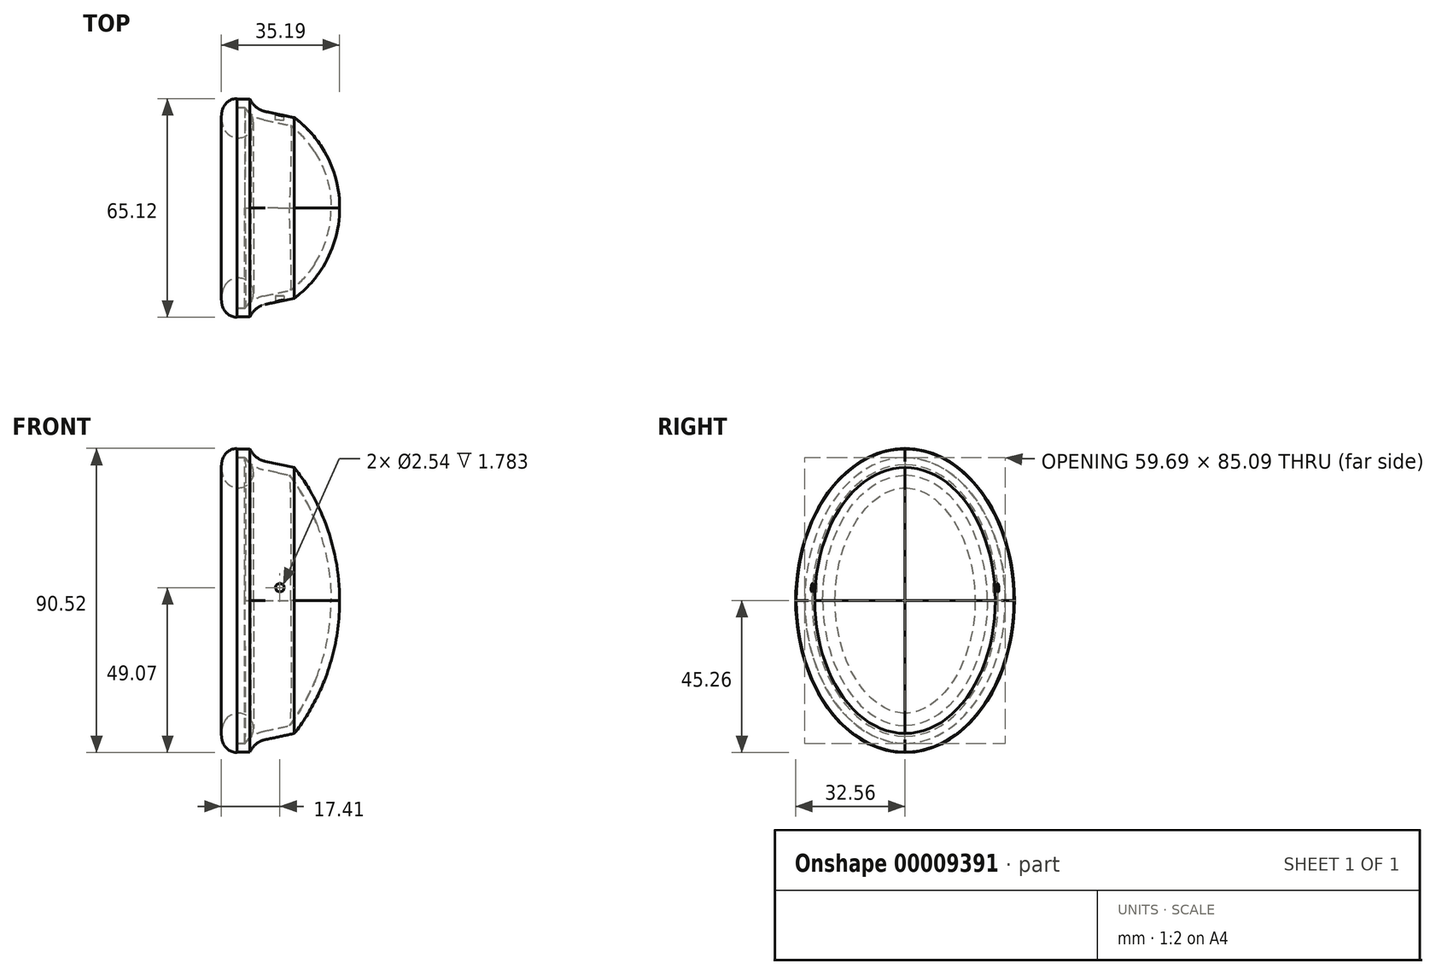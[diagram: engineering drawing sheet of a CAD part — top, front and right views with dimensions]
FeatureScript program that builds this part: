
annotation { "Feature Type Name" : "Feature", "Feature Type Description" : "" }
export const myFeature = defineFeature(function(context is Context, id is Id, definition is map)
    precondition{}
    {
        {
            var Q0;
            Q0=qCreatedBy(makeId("Front.planeOp"),FACE);
            var sketch = newSketch(context, id + "F0", { "sketchPlane" : qUnion([Q0])});
            skLineSegment(sketch, "E0", {"start": v(0, 45.09) * mm, "end": v(3.81, 45.09) * mm});
            skArc(sketch, "E1", {"start": v(3.81, 45.09) * mm, "mid": v(5.62, 42.7) * mm, "end": v(8.3, 41.41) * mm});
            skLineSegment(sketch, "E2", {"start": v(8.3, 41.41) * mm, "end": v(17, 39.57) * mm});
            skArc(sketch, "E3", {"start": v(30.48, 0) * mm, "mid": v(27.02, 20.9) * mm, "end": v(17, 39.57) * mm});
            skLineSegment(sketch, "E4", {"start": v(-135.5, 0) * mm, "end": v(142.56, 0) * mm, "construction": true});
            skLineSegment(sketch, "E5", {"start": v(0, 45.09) * mm, "end": v(0, 0) * mm});
            skLineSegment(sketch, "E6", {"start": v(30.48, 0) * mm, "end": v(0, 0) * mm});
            skSolve(sketch);
        }
        {
            var Q0;
            Q0=qCreatedBy(makeId("Right.planeOp"),FACE);
            var sketch = newSketch(context, id + "F1", { "sketchPlane" : qUnion([Q0])});
            skEllipticalArc(sketch, "E7", {});
            skLineSegment(sketch, "E8", {"start": v(-44.2, 0) * mm, "end": v(67.96, 0) * mm, "construction": true});
            skLineSegment(sketch, "E9", {"start": v(0, 0) * mm, "end": v(0, 53.19) * mm, "construction": true});
            const initialGuessF1  = {"E7": [0, 0, 0, 1, 0.045085, 0.032385, 0, 1.5707963267948966]};
            skSetInitialGuess(sketch, initialGuessF1);
            skSolve(sketch);
        }
        {
            var Q0;
            Q0=qCreatedBy(makeId("Top.planeOp"),FACE);
            var sketch = newSketch(context, id + "F2", { "sketchPlane" : qUnion([Q0])});
            skLineSegment(sketch, "E10", {"start": v(0, 0) * mm, "end": v(0, -32.39) * mm});
            skLineSegment(sketch, "E11", {"start": v(0, -32.39) * mm, "end": v(3.81, -32.39) * mm});
            skArc(sketch, "E12", {"start": v(8.3, -28.71) * mm, "mid": v(5.62, -30) * mm, "end": v(3.81, -32.39) * mm});
            skLineSegment(sketch, "E13", {"start": v(8.3, -28.71) * mm, "end": v(17, -26.87) * mm});
            skArc(sketch, "E14", {"start": v(17, -26.87) * mm, "mid": v(26.92, -15.03) * mm, "end": v(30.48, 0) * mm});
            skLineSegment(sketch, "E15", {"start": v(30.48, 0) * mm, "end": v(0, 0) * mm});
            skSolve(sketch);
        }
        {
            var Q0;
            Q0=qCreatedBy(makeId("Right.planeOp"),FACE);
            var Q1;
            Q1=sQuery(id+"F0.wireOp",VERTEX,"E1.start");
            cPlane(context, id + "F3", {"entities" : qUnion([Q0, Q1]), "cplaneType" : CPlaneType.PLANE_POINT, "offset" : 152.4 * mm, "width" : 152.4 * mm, "height" : 152.4 * mm});
        }
        {
            var Q0;
            Q0=qCreatedBy(id+"F3.planeOp",FACE);
            var sketch = newSketch(context, id + "F4", { "sketchPlane" : qUnion([Q0])});
            skEllipticalArc(sketch, "E16", {});
            skLineSegment(sketch, "E17", {"start": v(0, 0) * mm, "end": v(-53.23, 0) * mm, "construction": true});
            skLineSegment(sketch, "E18", {"start": v(0, 0) * mm, "end": v(0, 51.02) * mm, "construction": true});
            const initialGuessF4  = {"E16": [0, 0, 0, 1, 0.045085, 0.032385, 0, 1.5707963267948966]};
            skSetInitialGuess(sketch, initialGuessF4);
            skSolve(sketch);
        }
        {
            var Q0;
            Q0=qCreatedBy(id+"F3.planeOp",FACE);
            var Q1;
            Q1=sQuery(id+"F0.wireOp",VERTEX,"E2.start");
            cPlane(context, id + "F5", {"entities" : qUnion([Q0, Q1]), "cplaneType" : CPlaneType.PLANE_POINT, "offset" : 152.4 * mm, "width" : 152.4 * mm, "height" : 152.4 * mm});
        }
        {
            var Q0;
            Q0=qCreatedBy(id+"F5.planeOp",FACE);
            var sketch = newSketch(context, id + "F6", { "sketchPlane" : qUnion([Q0])});
            skEllipticalArc(sketch, "E19", {});
            skLineSegment(sketch, "E20.0", {"start": v(0, 0) * mm, "end": v(-53.23, 0) * mm, "construction": true});
            skLineSegment(sketch, "E21.0", {"start": v(0, 0) * mm, "end": v(0, 51.02) * mm, "construction": true});
            const initialGuessF6  = {"E19": [0, 0, 0, 1, 0.04141376273534034, 0.028713762735340338, 0, 1.5707963267948966]};
            skSetInitialGuess(sketch, initialGuessF6);
            skSolve(sketch);
        }
        {
            var Q0;
            Q0=sQuery(id+"F2.wireOp",VERTEX,"E14.start");
            var Q1;
            Q1=qCreatedBy(id+"F5.planeOp",FACE);
            cPlane(context, id + "F7", {"entities" : qUnion([Q0, Q1]), "cplaneType" : CPlaneType.PLANE_POINT, "offset" : 152.4 * mm, "width" : 152.4 * mm, "height" : 152.4 * mm});
        }
        {
            var Q0;
            Q0=qCreatedBy(id+"F7.planeOp",FACE);
            var sketch = newSketch(context, id + "F8", { "sketchPlane" : qUnion([Q0])});
            skEllipticalArc(sketch, "E22", {});
            skLineSegment(sketch, "E23.0", {"start": v(0, 0) * mm, "end": v(-53.23, 0) * mm, "construction": true});
            skLineSegment(sketch, "E23.1", {"start": v(0, 0) * mm, "end": v(0, 51.02) * mm, "construction": true});
            const initialGuessF8  = {"E22": [0, 0, 0, 1, 0.03956542780397045, 0.026865427803970467, 0, 1.5707963267948966]};
            skSetInitialGuess(sketch, initialGuessF8);
            skSolve(sketch);
        }
        {
            var Q0;
            Q0=makeQuery(id+"F0.imprint","IMPRINT",FACE,{"disambiguationData":[TD([[makeQuery(id+"F0.imprint","IMPRINT",EDGE,{"derivedFrom":sQuery(id+"F0.wireOp",EDGE,"E0")}),-1.0]])]});
            var Q1;
            Q1=makeQuery(id+"F2.imprint","IMPRINT",FACE,{"disambiguationData":[TD([[makeQuery(id+"F2.imprint","IMPRINT",EDGE,{"derivedFrom":sQuery(id+"F2.wireOp",EDGE,"E10")}),1.0]])]});
            var Q2;
            Q2=sQuery(id+"F1.wireOp",EDGE,"E7");
            var Q3;
            Q3=sQuery(id+"F4.wireOp",EDGE,"E16");
            var Q4;
            Q4=sQuery(id+"F6.wireOp",EDGE,"E19");
            var Q5;
            Q5=sQuery(id+"F8.wireOp",EDGE,"E22");
            loft(context, id + "F9", {"addGuides" : true, "sheetProfilesArray" : [{ "sheetProfileEntities" : qUnion([Q0]) }, { "sheetProfileEntities" : qUnion([Q1]) }], "guidesArray" : [{ "guideEntities" : qUnion([Q2]), "guideDerivativeType" : LoftGuideDerivativeType.DEFAULT, "guideDerivativeMagnitude" : 1 }, { "guideEntities" : qUnion([Q3]), "guideDerivativeType" : LoftGuideDerivativeType.DEFAULT, "guideDerivativeMagnitude" : 1 }, { "guideEntities" : qUnion([Q4]), "guideDerivativeType" : LoftGuideDerivativeType.DEFAULT, "guideDerivativeMagnitude" : 1 }, { "guideEntities" : qUnion([Q5]), "guideDerivativeType" : LoftGuideDerivativeType.DEFAULT, "guideDerivativeMagnitude" : 1 }]});
        }
        {
            var Q0;
            Q0=makeQuery(id+"F9.opLoft","SWEPT_BODY",BODY,{"disambiguationData":[OSD([makeQuery(id+"F0.imprint","IMPRINT",FACE,{"disambiguationData":[TD([[makeQuery(id+"F0.imprint","IMPRINT",EDGE,{"derivedFrom":sQuery(id+"F0.wireOp",EDGE,"E0")}),-1.0]])]}),sQuery(id+"F1.wireOp",EDGE,"E7"),makeQuery(id+"F2.imprint","IMPRINT",FACE,{"disambiguationData":[TD([[makeQuery(id+"F2.imprint","IMPRINT",EDGE,{"derivedFrom":sQuery(id+"F2.wireOp",EDGE,"E10")}),1.0]])]}),sQuery(id+"F4.wireOp",EDGE,"E16"),sQuery(id+"F6.wireOp",EDGE,"E19"),sQuery(id+"F8.wireOp",EDGE,"E22")])]});
            var Q1;
            Q1=qCreatedBy(makeId("Front.planeOp"),FACE);
            mirror(context, id + "F10", {"entities" : qUnion([Q0]), "mirrorPlane" : qUnion([Q1])});
        }
        {
            var Q0;
            Q0=makeQuery(id+"F9.opLoft","SWEPT_BODY",BODY,{"disambiguationData":[OSD([makeQuery(id+"F0.imprint","IMPRINT",FACE,{"disambiguationData":[TD([[makeQuery(id+"F0.imprint","IMPRINT",EDGE,{"derivedFrom":sQuery(id+"F0.wireOp",EDGE,"E0")}),-1.0]])]}),sQuery(id+"F1.wireOp",EDGE,"E7"),makeQuery(id+"F2.imprint","IMPRINT",FACE,{"disambiguationData":[TD([[makeQuery(id+"F2.imprint","IMPRINT",EDGE,{"derivedFrom":sQuery(id+"F2.wireOp",EDGE,"E10")}),1.0]])]}),sQuery(id+"F4.wireOp",EDGE,"E16"),sQuery(id+"F6.wireOp",EDGE,"E19"),sQuery(id+"F8.wireOp",EDGE,"E22")])]});
            var Q1;
            Q1=makeQuery(id+"F10.opPattern","COPY",BODY,{"derivedFrom":makeQuery(id+"F9.opLoft","SWEPT_BODY",BODY,{"disambiguationData":[OSD([makeQuery(id+"F0.imprint","IMPRINT",FACE,{"disambiguationData":[TD([[makeQuery(id+"F0.imprint","IMPRINT",EDGE,{"derivedFrom":sQuery(id+"F0.wireOp",EDGE,"E0")}),-1.0]])]}),sQuery(id+"F1.wireOp",EDGE,"E7"),makeQuery(id+"F2.imprint","IMPRINT",FACE,{"disambiguationData":[TD([[makeQuery(id+"F2.imprint","IMPRINT",EDGE,{"derivedFrom":sQuery(id+"F2.wireOp",EDGE,"E10")}),1.0]])]}),sQuery(id+"F4.wireOp",EDGE,"E16"),sQuery(id+"F6.wireOp",EDGE,"E19"),sQuery(id+"F8.wireOp",EDGE,"E22")])]}),"instanceName":"1"});
            var Q2;
            Q2=qCreatedBy(makeId("Top.planeOp"),FACE);
            mirror(context, id + "F11", {"entities" : qUnion([Q0, Q1]), "mirrorPlane" : qUnion([Q2])});
        }
        {
            var Q0;
            Q0=makeQuery(id+"F10.opPattern","COPY",BODY,{"derivedFrom":makeQuery(id+"F9.opLoft","SWEPT_BODY",BODY,{"disambiguationData":[OSD([makeQuery(id+"F0.imprint","IMPRINT",FACE,{"disambiguationData":[TD([[makeQuery(id+"F0.imprint","IMPRINT",EDGE,{"derivedFrom":sQuery(id+"F0.wireOp",EDGE,"E0")}),-1.0]])]}),sQuery(id+"F1.wireOp",EDGE,"E7"),makeQuery(id+"F2.imprint","IMPRINT",FACE,{"disambiguationData":[TD([[makeQuery(id+"F2.imprint","IMPRINT",EDGE,{"derivedFrom":sQuery(id+"F2.wireOp",EDGE,"E10")}),1.0]])]}),sQuery(id+"F4.wireOp",EDGE,"E16"),sQuery(id+"F6.wireOp",EDGE,"E19"),sQuery(id+"F8.wireOp",EDGE,"E22")])]}),"instanceName":"1"});
            var Q1;
            Q1=makeQuery(id+"F9.opLoft","SWEPT_BODY",BODY,{"disambiguationData":[OSD([makeQuery(id+"F0.imprint","IMPRINT",FACE,{"disambiguationData":[TD([[makeQuery(id+"F0.imprint","IMPRINT",EDGE,{"derivedFrom":sQuery(id+"F0.wireOp",EDGE,"E0")}),-1.0]])]}),sQuery(id+"F1.wireOp",EDGE,"E7"),makeQuery(id+"F2.imprint","IMPRINT",FACE,{"disambiguationData":[TD([[makeQuery(id+"F2.imprint","IMPRINT",EDGE,{"derivedFrom":sQuery(id+"F2.wireOp",EDGE,"E10")}),1.0]])]}),sQuery(id+"F4.wireOp",EDGE,"E16"),sQuery(id+"F6.wireOp",EDGE,"E19"),sQuery(id+"F8.wireOp",EDGE,"E22")])]});
            var Q2;
            Q2=makeQuery(id+"F11.opPattern","COPY",BODY,{"derivedFrom":makeQuery(id+"F9.opLoft","SWEPT_BODY",BODY,{"disambiguationData":[OSD([makeQuery(id+"F0.imprint","IMPRINT",FACE,{"disambiguationData":[TD([[makeQuery(id+"F0.imprint","IMPRINT",EDGE,{"derivedFrom":sQuery(id+"F0.wireOp",EDGE,"E0")}),-1.0]])]}),sQuery(id+"F1.wireOp",EDGE,"E7"),makeQuery(id+"F2.imprint","IMPRINT",FACE,{"disambiguationData":[TD([[makeQuery(id+"F2.imprint","IMPRINT",EDGE,{"derivedFrom":sQuery(id+"F2.wireOp",EDGE,"E10")}),1.0]])]}),sQuery(id+"F4.wireOp",EDGE,"E16"),sQuery(id+"F6.wireOp",EDGE,"E19"),sQuery(id+"F8.wireOp",EDGE,"E22")])]}),"instanceName":"1"});
            var Q3;
            Q3=makeQuery(id+"F11.opPattern","COPY",BODY,{"derivedFrom":makeQuery(id+"F10.opPattern","COPY",BODY,{"derivedFrom":makeQuery(id+"F9.opLoft","SWEPT_BODY",BODY,{"disambiguationData":[OSD([makeQuery(id+"F0.imprint","IMPRINT",FACE,{"disambiguationData":[TD([[makeQuery(id+"F0.imprint","IMPRINT",EDGE,{"derivedFrom":sQuery(id+"F0.wireOp",EDGE,"E0")}),-1.0]])]}),sQuery(id+"F1.wireOp",EDGE,"E7"),makeQuery(id+"F2.imprint","IMPRINT",FACE,{"disambiguationData":[TD([[makeQuery(id+"F2.imprint","IMPRINT",EDGE,{"derivedFrom":sQuery(id+"F2.wireOp",EDGE,"E10")}),1.0]])]}),sQuery(id+"F4.wireOp",EDGE,"E16"),sQuery(id+"F6.wireOp",EDGE,"E19"),sQuery(id+"F8.wireOp",EDGE,"E22")])]}),"instanceName":"1"}),"instanceName":"1"});
            booleanBodies(context, id + "F12", {"operationType" : BooleanOperationType.UNION, "tools" : qUnion([Q0, Q1, Q2, Q3])});
        }
        {
            var Q0;
            {var subQ0=makeQuery(id+"F9.opLoft","SWEPT_FACE",FACE,{"disambiguationData":[OSD([sQuery(id+"F0.wireOp",EDGE,"E5"),sQuery(id+"F0.wireOp",EDGE,"E6"),sQuery(id+"F1.wireOp",EDGE,"E7"),sQuery(id+"F2.wireOp",EDGE,"E10"),sQuery(id+"F2.wireOp",EDGE,"E11"),sQuery(id+"F2.wireOp",EDGE,"E15")])]});var subQ1=makeQuery(id+"F10.opPattern","COPY",FACE,{"derivedFrom":subQ0,"instanceName":"1"});Q0=makeQuery(id+"F12.opBoolean","MERGE",FACE,{"derivedFrom":[subQ0,subQ1,makeQuery(id+"F11.opPattern","COPY",FACE,{"derivedFrom":subQ0,"instanceName":"1"}),makeQuery(id+"F11.opPattern","COPY",FACE,{"derivedFrom":subQ1,"instanceName":"1"})]});}
            shell(context, id + "F13", {"entities" : qUnion([Q0]), "thickness" : 2.54 * mm});
        }
        {
            var Q0;
            Q0=qCreatedBy(makeId("Front.planeOp"),FACE);
            var sketch = newSketch(context, id + "F14", { "sketchPlane" : qUnion([Q0])});
            skPoint(sketch, "E24.orphan", {"position": v(6.31, 39.38) * mm});
            skArc(sketch, "E25", {"start": v(0, 45.26) * mm, "mid": v(-2.72, 44.36) * mm, "end": v(-4.37, 42) * mm});
            skArc(sketch, "E26", {"start": v(-4.37, 42) * mm, "mid": v(-4.65, 38.82) * mm, "end": v(-3.64, 35.78) * mm});
            skArc(sketch, "E27", {"start": v(-3.64, 35.78) * mm, "mid": v(2.62, 34.16) * mm, "end": v(4.17, 40.43) * mm});
            skLineSegment(sketch, "E28.0", {"start": v(0, 45.26) * mm, "end": v(0, 42.51) * mm});
            skFitSpline(sketch, "E28.2", {"points": [v(6.3, 39.2) * mm, v(6.18, 39.26) * mm, v(5.93, 39.36) * mm, v(5.44, 39.6) * mm, v(4.86, 39.93) * mm, v(4.2, 40.4) * mm, v(3.58, 40.92) * mm, v(3, 41.5) * mm, v(2.32, 42.33) * mm, v(1.9, 43.02) * mm, v(1.65, 43.51) * mm]});
            skLineSegment(sketch, "E29", {"start": v(2.23, 42.51) * mm, "end": v(0, 42.51) * mm});
            skSolve(sketch);
        }
        {
            var Q0;
            Q0 = qSketchRegion(id + "F14", true);
            var Q1;
            {var subQ0=sQuery(id+"F1.wireOp",EDGE,"E7");Q1=makeQuery(id+"F13.opShell","OFFSET_EDGE",EDGE,{"disambiguationData":[OSD([subQ0]),TDD([makeQuery(id+"F10.opPattern","COPY",EDGE,{"derivedFrom":makeQuery(id+"F9.opLoft","SWEPT_EDGE",EDGE,{"disambiguationData":[OSD([subQ0])]}),"instanceName":"1"})])]});}
            var Q2;
            {var subQ0=sQuery(id+"F1.wireOp",EDGE,"E7");Q2=makeQuery(id+"F13.opShell","OFFSET_EDGE",EDGE,{"disambiguationData":[OSD([subQ0]),TDD([makeQuery(id+"F11.opPattern","COPY",EDGE,{"derivedFrom":makeQuery(id+"F10.opPattern","COPY",EDGE,{"derivedFrom":makeQuery(id+"F9.opLoft","SWEPT_EDGE",EDGE,{"disambiguationData":[OSD([subQ0])]}),"instanceName":"1"}),"instanceName":"1"})])]});}
            var Q3;
            {var subQ0=sQuery(id+"F1.wireOp",EDGE,"E7");Q3=makeQuery(id+"F13.opShell","OFFSET_EDGE",EDGE,{"disambiguationData":[OSD([subQ0]),TDD([makeQuery(id+"F11.opPattern","COPY",EDGE,{"derivedFrom":makeQuery(id+"F9.opLoft","SWEPT_EDGE",EDGE,{"disambiguationData":[OSD([subQ0])]}),"instanceName":"1"})])]});}
            var Q4;
            {var subQ0=sQuery(id+"F1.wireOp",EDGE,"E7");Q4=makeQuery(id+"F13.opShell","OFFSET_EDGE",EDGE,{"disambiguationData":[OSD([subQ0]),TDD([makeQuery(id+"F9.opLoft","SWEPT_EDGE",EDGE,{"disambiguationData":[OSD([subQ0])]})])]});}
            sweep(context, id + "F15", {"profiles" : qUnion([Q0]), "path" : qUnion([Q1, Q2, Q3, Q4])});
        }
        {
            var Q0;
            Q0=qCreatedBy(makeId("Front.planeOp"),FACE);
            cPlane(context, id + "F16", {"entities" : qUnion([Q0]), "cplaneType" : CPlaneType.OFFSET, "offset" : 33.02 * mm, "width" : 152.4 * mm, "height" : 152.4 * mm});
        }
        {
            var Q0;
            Q0=qCreatedBy(id+"F16.planeOp",FACE);
            var sketch = newSketch(context, id + "F17", { "sketchPlane" : qUnion([Q0])});
            skCircle(sketch, "E30", {"center": v(12.7, 3.81) * mm, "radius": 1.27 * mm});
            skSolve(sketch);
        }
        {
            var Q0;
            Q0=makeQuery(id+"F17.imprint","IMPRINT",FACE,{"disambiguationData":[TD([[makeQuery(id+"F17.imprint","IMPRINT",EDGE,{"derivedFrom":sQuery(id+"F17.wireOp",EDGE,"E30")}),1.0]])]});
            extrude(context, id + "F18", {"entities" : qUnion([Q0]), "operationType" : NewBodyOperationType.REMOVE, "oppositeDirection" : true, "depth" : 6.86 * mm});
        }
        {
            var Q0;
            Q0=qCreatedBy(makeId("Front.planeOp"),FACE);
            cPlane(context, id + "F19", {"entities" : qUnion([Q0]), "cplaneType" : CPlaneType.OFFSET, "offset" : 33.02 * mm, "oppositeDirection" : true, "width" : 152.4 * mm, "height" : 152.4 * mm});
        }
        {
            var Q0;
            Q0=qCreatedBy(id+"F19.planeOp",FACE);
            var sketch = newSketch(context, id + "F20", { "sketchPlane" : qUnion([Q0])});
            skCircle(sketch, "E31", {"center": v(12.7, 3.81) * mm, "radius": 1.27 * mm});
            skSolve(sketch);
        }
        {
            var Q0;
            Q0=makeQuery(id+"F20.imprint","IMPRINT",FACE,{"disambiguationData":[TD([[makeQuery(id+"F20.imprint","IMPRINT",EDGE,{"derivedFrom":sQuery(id+"F20.wireOp",EDGE,"E31")}),1.0]])]});
            extrude(context, id + "F21", {"entities" : qUnion([Q0]), "operationType" : NewBodyOperationType.REMOVE, "depth" : 6.86 * mm});
        }
    });
